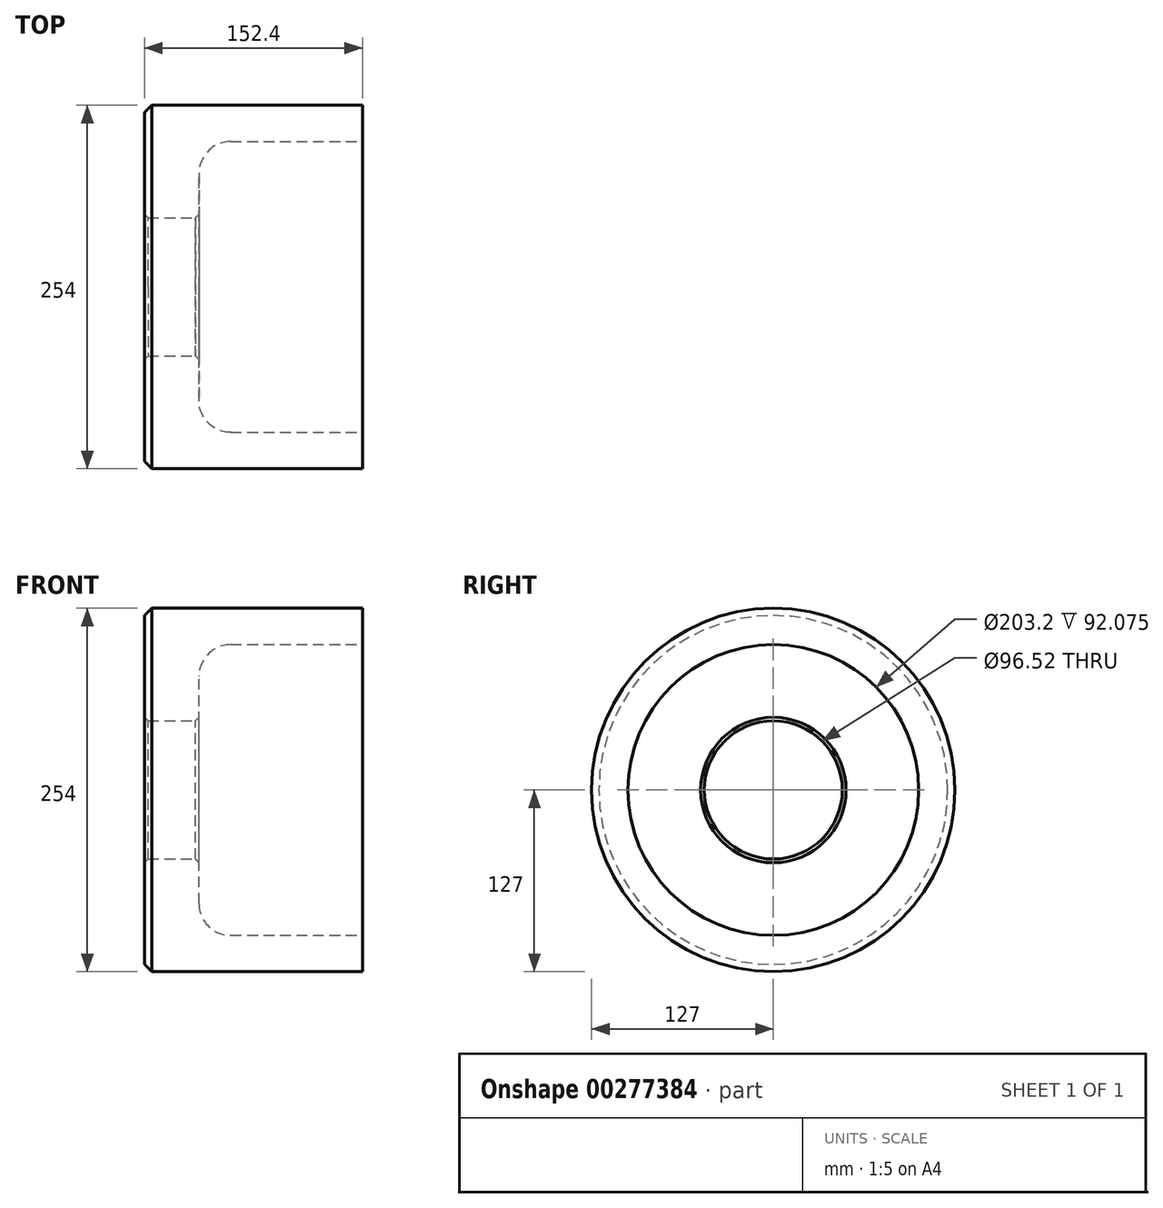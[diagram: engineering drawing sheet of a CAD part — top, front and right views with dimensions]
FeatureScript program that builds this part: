
annotation { "Feature Type Name" : "Feature", "Feature Type Description" : "" }
export const myFeature = defineFeature(function(context is Context, id is Id, definition is map)
    precondition{}
    {
        {
            var Q0;
            Q0=qCreatedBy(makeId("Front.planeOp"),FACE);
            var sketch = newSketch(context, id + "F0", { "sketchPlane" : qUnion([Q0])});
            skLineSegment(sketch, "E0", {"start": v(58.27, 0) * mm, "end": v(-201.7, 0) * mm, "construction": true});
            skLineSegment(sketch, "E1", {"start": v(0, 127) * mm, "end": v(-152.4, 127) * mm});
            skLineSegment(sketch, "E2", {"start": v(-152.4, 127) * mm, "end": v(-152.4, 48.26) * mm});
            skLineSegment(sketch, "E3", {"start": v(-152.4, 48.26) * mm, "end": v(-114.3, 48.26) * mm});
            skLineSegment(sketch, "E4", {"start": v(-114.3, 48.26) * mm, "end": v(-114.3, 79.37) * mm});
            skLineSegment(sketch, "E5", {"start": v(-92.08, 101.6) * mm, "end": v(0, 101.6) * mm});
            skLineSegment(sketch, "E6", {"start": v(0, 101.6) * mm, "end": v(0, 127) * mm});
            skArc(sketch, "E7", {"start": v(-114.3, 79.37) * mm, "mid": v(-107.8, 95.1) * mm, "end": v(-92.08, 101.6) * mm});
            skSolve(sketch);
        }
        {
            var Q0;
            Q0=makeQuery(id+"F0.imprint","IMPRINT",FACE,{"disambiguationData":[TD([[makeQuery(id+"F0.imprint","IMPRINT",EDGE,{"derivedFrom":sQuery(id+"F0.wireOp",EDGE,"E1")}),1.0]])]});
            var Q1;
            Q1=sQuery(id+"F0.wireOp",EDGE,"E0");
            revolve(context, id + "F1", {"entities" : qUnion([Q0]), "axis" : qUnion([Q1]), "revolveType" : RevolveType.FULL});
        }
        {
            var Q0;
            Q0=makeQuery(id+"F1.opRevolve","SWEPT_EDGE",EDGE,{"disambiguationData":[OSD([sQuery(id+"F0.wireOp",EDGE,"E1"),sQuery(id+"F0.wireOp",EDGE,"E2")])]});
            chamfer(context, id + "F2", {"entities" : qUnion([Q0]), "width" : 5.08 * mm, "tangentPropagation" : true});
        }
        {
            var Q0;
            Q0=makeQuery(id+"F1.opRevolve","SWEPT_FACE",FACE,{"disambiguationData":[OSD([sQuery(id+"F0.wireOp",EDGE,"E3")])]});
            chamfer(context, id + "F3", {"entities" : qUnion([Q0]), "width" : 2.54 * mm, "tangentPropagation" : true});
        }
    });
